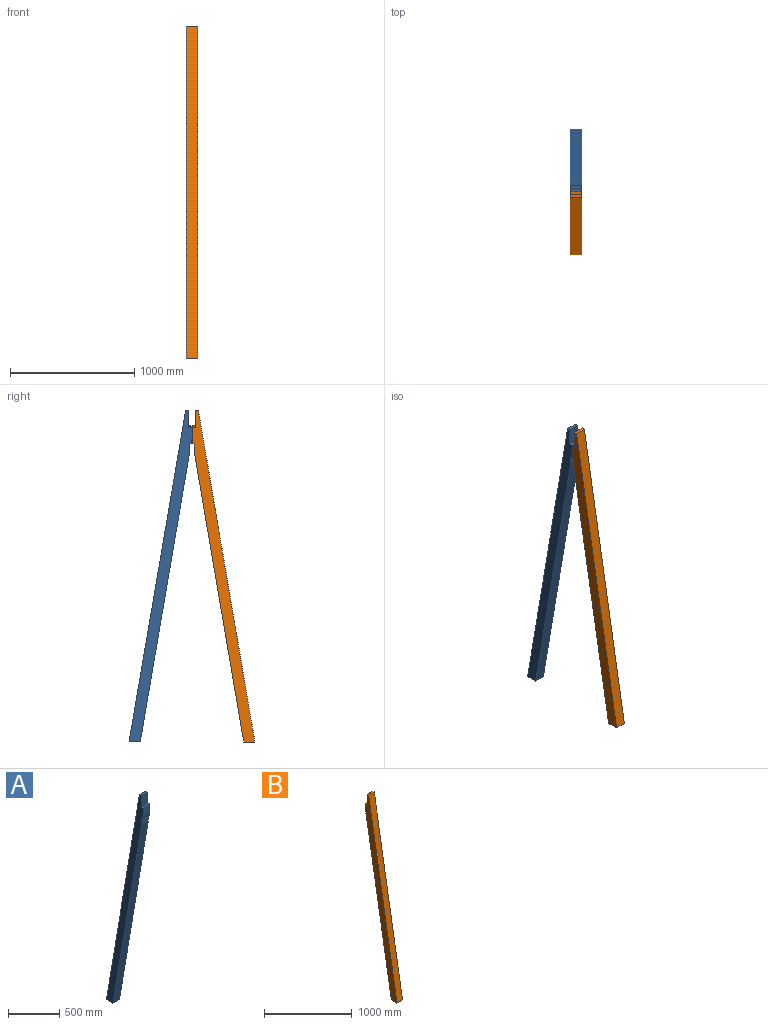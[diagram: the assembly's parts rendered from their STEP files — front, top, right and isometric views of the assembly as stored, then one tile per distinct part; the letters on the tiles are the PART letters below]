
ASSEMBLY  parts=2 mates=1
PART A: 12 faces, bbox 88.9x505.8x2669.5 mm
  f0: plane 88.9x40.63mm, normal (0,-0.99,-0.17), area 3664.1mm2, adj f1,f2,f6,f11
  f1: plane 2669.46x505.78mm, normal (1,0,0), area 232495.4mm2, adj f0,f3,f4,f5,f6,f7,f8,f9
  f2: plane 2669.46x505.78mm, normal (-1,0,0), area 232270.4mm2, adj f0,f3,f4,f5,f6,f7,f8,f9
  f3: plane 2669.46x454.98mm, normal (0,0.99,0.17), area 240737.4mm2, adj f1,f2,f4,f8
  f4: plane 90.18x88.9mm, normal (0,0,-1), area 8017.2mm2, adj f1,f2,f3,f5
  f5: plane 2326.63x396.55mm, normal (0,-0.99,-0.17), area 209820.2mm2, adj f1,f2,f4,f10
  f6: plane 102.68x88.9mm, normal (0,-1,0), area 8723mm2, adj f0,f1,f2,f9
  f7: plane 137.24x88.9mm, normal (0,-1,0), area 11818.4mm2, adj f1,f2,f8,f9
  f8: plane 88.9x25.4mm, normal (0,0,1), area 2258.1mm2, adj f1,f2,f3,f7
  f9: cylinder r=5251.45mm len=88.9mm, axis (0,-1,0), area 2269.3mm2, adj f1,f2,f6,f7
  f10: plane 88.9x71.14mm, normal (0,-1,0), area 6324.4mm2, adj f1,f2,f5,f11
  f11: plane 88.9x12.13mm, normal (0,0,-1), area 1077.9mm2, adj f0,f1,f2,f10
PART B: 12 faces, bbox 88.9x505.8x2669.5 mm
  f0: plane 88.9x40.63mm, normal (0,0.99,-0.17), area 3664.1mm2, adj f1,f2,f6,f11
  f1: plane 2669.46x505.78mm, normal (1,0,0), area 232495.4mm2, adj f0,f3,f4,f5,f6,f7,f8,f9
  f2: plane 2669.46x505.78mm, normal (-1,0,0), area 232270.4mm2, adj f0,f3,f4,f5,f6,f7,f8,f9
  f3: plane 2669.46x454.98mm, normal (0,-0.99,0.17), area 240737.4mm2, adj f1,f2,f4,f8
  f4: plane 90.18x88.9mm, normal (0,0,-1), area 8017.2mm2, adj f1,f2,f3,f5
  f5: plane 2326.63x396.55mm, normal (0,0.99,-0.17), area 209820.2mm2, adj f1,f2,f4,f10
  f6: plane 102.68x88.9mm, normal (0,1,0), area 8723mm2, adj f0,f1,f2,f9
  f7: plane 137.24x88.9mm, normal (0,1,0), area 11818.4mm2, adj f1,f2,f8,f9
  f8: plane 88.9x25.4mm, normal (0,0,1), area 2258.1mm2, adj f1,f2,f3,f7
  f9: cylinder r=5251.45mm len=88.9mm, axis (0,1,0), area 2269.3mm2, adj f1,f2,f6,f7
  f10: plane 88.9x71.14mm, normal (0,1,0), area 6324.4mm2, adj f1,f2,f5,f11
  f11: plane 88.9x12.13mm, normal (0,0,-1), area 1077.9mm2, adj f0,f1,f2,f10
PLACE A t=(-44.45,460.64,0)mm
PLACE B t=(-44.45,460.69,0)mm
MATE fastened A.f6 <-> B.f6  axis (0,-1,0) through (-44.45,460.69,2532.22)mm
